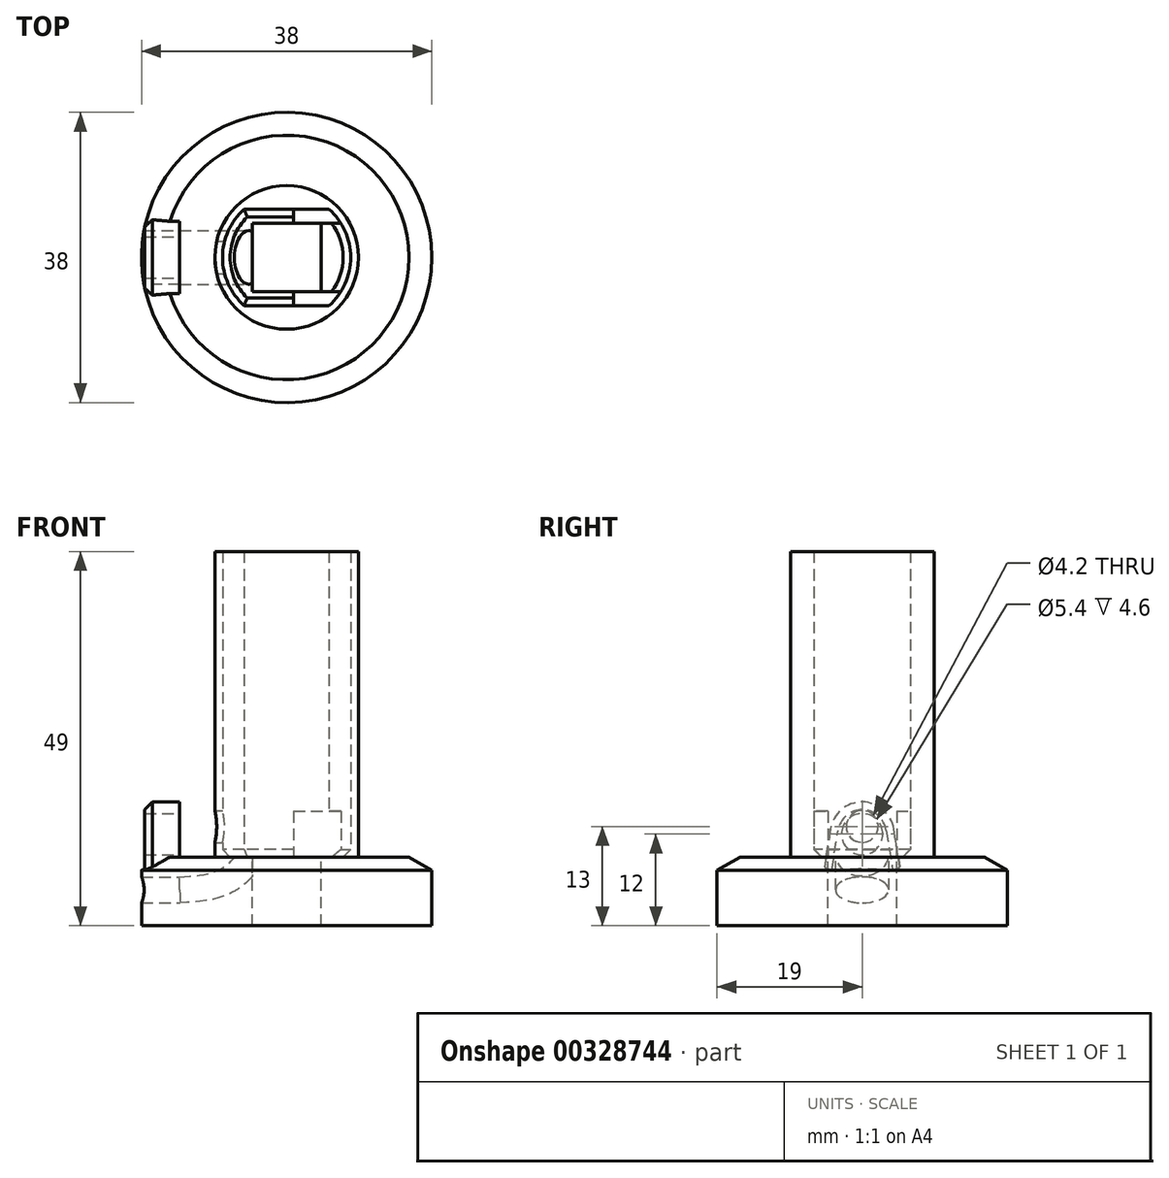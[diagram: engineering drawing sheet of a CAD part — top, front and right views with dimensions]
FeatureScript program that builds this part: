
annotation { "Feature Type Name" : "Feature", "Feature Type Description" : "" }
export const myFeature = defineFeature(function(context is Context, id is Id, definition is map)
    precondition{}
    {
        {
            var Q0;
            Q0=qCreatedBy(makeId("Top.planeOp"),FACE);
            var sketch = newSketch(context, id + "F0", { "sketchPlane" : qUnion([Q0])});
            skArc(sketch, "E0", {"start": v(-5.56, 6.3) * mm, "mid": v(-8.4, 0) * mm, "end": v(-5.56, -6.3) * mm});
            skLineSegment(sketch, "E1", {"start": v(-5.56, -6.3) * mm, "end": v(5.56, -6.3) * mm});
            skLineSegment(sketch, "E2", {"start": v(5.56, 6.3) * mm, "end": v(-5.56, 6.3) * mm});
            skArc(sketch, "E3.trimOffspring", {"start": v(5.56, -6.3) * mm, "mid": v(8.4, 0) * mm, "end": v(5.56, 6.3) * mm});
            skCircle(sketch, "E4", {"center": v(0, 0) * mm, "radius": 9.4 * mm});
            skSolve(sketch);
        }
        {
            var Q0;
            Q0 = qSketchRegion(id + "F0", true);
            extrude(context, id + "F1", {"entities" : qUnion([Q0]), "depth" : 40 * mm});
        }
        {
            var Q0;
            Q0=qCreatedBy(makeId("Top.planeOp"),FACE);
            var sketch = newSketch(context, id + "F2", { "sketchPlane" : qUnion([Q0])});
            skCircle(sketch, "E5", {"center": v(0, 0) * mm, "radius": 19 * mm});
            skLineSegment(sketch, "E6.bottom", {"start": v(-4.5, 4.5) * mm, "end": v(4.5, 4.5) * mm});
            skLineSegment(sketch, "E6.top", {"start": v(-4.5, -4.5) * mm, "end": v(4.5, -4.5) * mm});
            skLineSegment(sketch, "E6.left", {"start": v(-4.5, 4.5) * mm, "end": v(-4.5, -4.5) * mm});
            skLineSegment(sketch, "E6.right", {"start": v(4.5, 4.5) * mm, "end": v(4.5, -4.5) * mm});
            skLineSegment(sketch, "E7", {"start": v(-4.5, 4.5) * mm, "end": v(4.5, -4.5) * mm, "construction": true});
            skSolve(sketch);
        }
        {
            var Q0;
            Q0 = qSketchRegion(id + "F2", true);
            extrude(context, id + "F3", {"entities" : qUnion([Q0]), "operationType" : NewBodyOperationType.ADD, "oppositeDirection" : true, "depth" : 9 * mm});
        }
        {
            var Q0;
            Q0=makeQuery(id+"F1.opExtrude","CAP_EDGE",EDGE,{"disambiguationData":[OSD([sQuery(id+"F0.wireOp",EDGE,"E0")])],"isStart":true});
            var Q1;
            Q1=makeQuery(id+"F1.opExtrude","CAP_EDGE",EDGE,{"disambiguationData":[OSD([sQuery(id+"F0.wireOp",EDGE,"E2")])],"isStart":true});
            var Q2;
            Q2=makeQuery(id+"F1.opExtrude","CAP_EDGE",EDGE,{"disambiguationData":[OSD([sQuery(id+"F0.wireOp",EDGE,"E3.trimOffspring")])],"isStart":true});
            var Q3;
            Q3=makeQuery(id+"F1.opExtrude","CAP_EDGE",EDGE,{"disambiguationData":[OSD([sQuery(id+"F0.wireOp",EDGE,"E1")])],"isStart":true});
            chamfer(context, id + "F4", {"entities" : qUnion([Q0, Q1, Q2, Q3]), "width" : 1 * mm, "tangentPropagation" : true});
        }
        {
            var Q0;
            Q0=qCreatedBy(makeId("Right.planeOp"),FACE);
            var sketch = newSketch(context, id + "F5", { "sketchPlane" : qUnion([Q0])});
            skCircle(sketch, "E8.cCircle", {"center": v(0, 4) * mm, "radius": 2.1 * mm});
            skSolve(sketch);
        }
        {
            var Q0;
            Q0 = qSketchRegion(id + "F5", true);
            extrude(context, id + "F6", {"entities" : qUnion([Q0]), "operationType" : NewBodyOperationType.REMOVE, "oppositeDirection" : true, "depth" : 25 * mm});
        }
        {
            var Q0;
            Q0=makeQuery(id+"F3.opExtrude","CAP_EDGE",EDGE,{"disambiguationData":[OSD([sQuery(id+"F2.wireOp",EDGE,"E5")])],"isStart":true});
            chamfer(context, id + "F7", {"entities" : qUnion([Q0]), "chamferType" : ChamferType.OFFSET_ANGLE, "width" : 3 * mm, "oppositeDirection" : false, "angle" : 30 * degree, "tangentPropagation" : true});
        }
        {
            var Q0;
            Q0=qCreatedBy(makeId("Right.planeOp"),FACE);
            cPlane(context, id + "F8", {"entities" : qUnion([Q0]), "cplaneType" : CPlaneType.OFFSET, "offset" : 19 * mm, "oppositeDirection" : true, "width" : 150 * mm, "height" : 150 * mm});
        }
        {
            var Q0;
            Q0=qCreatedBy(id+"F8.planeOp",FACE);
            var sketch = newSketch(context, id + "F9", { "sketchPlane" : qUnion([Q0])});
            skLineSegment(sketch, "E9", {"start": v(0, 0) * mm, "end": v(0, -4.3) * mm, "construction": true});
            skEllipse(sketch, "E10", {"center": v(0, -4.3) * mm, "majorRadius": 3.5 * mm, "minorRadius": 1.7 * mm, "majorAxis": v(-1, 0)});
            skSolve(sketch);
        }
        {
            var Q0;
            Q0=qCreatedBy(makeId("Front.planeOp"),FACE);
            var sketch = newSketch(context, id + "F10", { "sketchPlane" : qUnion([Q0])});
            skLineSegment(sketch, "E11", {"start": v(-19, -4.3) * mm, "end": v(-14, -4.3) * mm});
            skFitSpline(sketch, "E12", {"points": [v(-14, -4.3) * mm, v(-7.22, -2.71) * mm, v(-4.5, 0.94) * mm], "startDerivative": vector(22.35, 1.09) * mm, "endDerivative": vector(5.98, 14.7) * mm});
            skSolve(sketch);
        }
        {
            var Q0;
            Q0=makeQuery(id+"F9.imprint","IMPRINT",FACE,{"disambiguationData":[TD([[makeQuery(id+"F9.imprint","IMPRINT",EDGE,{"derivedFrom":sQuery(id+"F9.wireOp",EDGE,"E10")}),1.0]])]});
            var Q1;
            Q1=sQuery(id+"F10.wireOp",EDGE,"E11");
            var Q2;
            Q2=sQuery(id+"F10.wireOp",EDGE,"E12");
            sweep(context, id + "F11", {"operationType" : NewBodyOperationType.REMOVE, "profiles" : qUnion([Q0]), "path" : qUnion([Q1, Q2])});
        }
        {
            var Q0;
            Q0=qCreatedBy(makeId("Right.planeOp"),FACE);
            cPlane(context, id + "F12", {"entities" : qUnion([Q0]), "cplaneType" : CPlaneType.OFFSET, "offset" : 14 * mm, "oppositeDirection" : true, "width" : 150 * mm, "height" : 150 * mm});
        }
        {
            var Q0;
            Q0=qCreatedBy(id+"F12.planeOp",FACE);
            var sketch = newSketch(context, id + "F13", { "sketchPlane" : qUnion([Q0])});
            skLineSegment(sketch, "E13", {"start": v(0, 0) * mm, "end": v(0, 3) * mm});
            skCircle(sketch, "E14", {"center": v(0, 3) * mm, "radius": 2.7 * mm});
            skArc(sketch, "E15", {"start": v(4.15, 3.66) * mm, "mid": v(0, 7.2) * mm, "end": v(-4.15, 3.66) * mm});
            skLineSegment(sketch, "E16", {"start": v(0, 0) * mm, "end": v(0, -1.73) * mm});
            skLineSegment(sketch, "E17", {"start": v(5, -1.73) * mm, "end": v(-5, -1.73) * mm});
            skLineSegment(sketch, "E18", {"start": v(5, -1.73) * mm, "end": v(4.15, 3.66) * mm});
            skLineSegment(sketch, "E19", {"start": v(-5, -1.73) * mm, "end": v(-4.15, 3.66) * mm});
            skPoint(sketch, "E20.orphan", {"position": v(-4.2, 3) * mm});
            skPoint(sketch, "E21.orphan", {"position": v(4.2, 3) * mm});
            skSolve(sketch);
        }
        {
            var Q0;
            Q0 = qSketchRegion(id + "F13", true);
            extrude(context, id + "F14", {"entities" : qUnion([Q0]), "operationType" : NewBodyOperationType.ADD, "oppositeDirection" : true, "depth" : 4.6 * mm});
        }
        {
            var Q0;
            Q0=makeQuery(id+"F14.opExtrude","CAP_EDGE",EDGE,{"disambiguationData":[OSD([sQuery(id+"F13.wireOp",EDGE,"E15")])],"isStart":false});
            var Q1;
            Q1=makeQuery(id+"F14.opExtrude","CAP_EDGE",EDGE,{"disambiguationData":[OSD([sQuery(id+"F13.wireOp",EDGE,"mBPwjUWr-pTdr-WgdO-0FXO-sCMZVrisKc0V.left")])],"isStart":false});
            var Q2;
            Q2=makeQuery(id+"F14.opExtrude","CAP_EDGE",EDGE,{"disambiguationData":[OSD([sQuery(id+"F13.wireOp",EDGE,"mBPwjUWr-pTdr-WgdO-0FXO-sCMZVrisKc0V.right")])],"isStart":false});
            chamfer(context, id + "F15", {"entities" : qUnion([Q0, Q1, Q2]), "width" : 1 * mm, "tangentPropagation" : true});
        }
        {
            var Q0;
            {var subQ0=sQuery(id+"F2.wireOp",EDGE,"E5");Q0=makeQuery(id+"F3.boolean.opBoolean","SPLIT",FACE,{"disambiguationData":[TD([makeQuery(id+"F1.opExtrude","SWEPT_FACE",FACE,{"disambiguationData":[OSD([sQuery(id+"F0.wireOp",EDGE,"E4")])]})])],"derivedFrom":makeQuery(id+"F3.opExtrude","CAP_FACE",FACE,{"disambiguationData":[OSD([subQ0,sQuery(id+"F2.wireOp",EDGE,"E6.bottom"),sQuery(id+"F2.wireOp",EDGE,"E6.top"),sQuery(id+"F2.wireOp",EDGE,"E6.left"),sQuery(id+"F2.wireOp",EDGE,"E6.right")])],"isStart":true})});}
            cPlane(context, id + "F16", {"entities" : qUnion([Q0]), "cplaneType" : CPlaneType.OFFSET, "offset" : 0 * mm, "width" : 150 * mm, "height" : 150 * mm});
        }
        {
            var Q0;
            Q0=qCreatedBy(id+"F16.planeOp",FACE);
            var sketch = newSketch(context, id + "F17", { "sketchPlane" : qUnion([Q0])});
            skLineSegment(sketch, "E22.bottom", {"start": v(0.9, 4.5) * mm, "end": v(7.1, 4.5) * mm});
            skLineSegment(sketch, "E22.top", {"start": v(0.9, 6.3) * mm, "end": v(5.56, 6.3) * mm});
            skLineSegment(sketch, "E22.left", {"start": v(0.9, 4.5) * mm, "end": v(0.9, 6.3) * mm});
            skLineSegment(sketch, "E23", {"start": v(-40, 0) * mm, "end": v(47.05, 0) * mm, "construction": true});
            skLineSegment(sketch, "E24.MirrorCS", {"start": v(0.9, -4.5) * mm, "end": v(7.1, -4.5) * mm});
            skLineSegment(sketch, "E25.MirrorCS", {"start": v(0.9, -4.5) * mm, "end": v(0.9, -6.3) * mm});
            skLineSegment(sketch, "E26.MirrorCS", {"start": v(0.9, -6.3) * mm, "end": v(5.56, -6.3) * mm});
            skArc(sketch, "E27", {"start": v(5.56, -6.3) * mm, "mid": v(6.39, -5.45) * mm, "end": v(7.1, -4.5) * mm});
            skArc(sketch, "E28.trimOffspring", {"start": v(7.1, 4.5) * mm, "mid": v(6.39, 5.45) * mm, "end": v(5.56, 6.3) * mm});
            skSolve(sketch);
        }
        {
            var Q0;
            Q0 = qSketchRegion(id + "F17", true);
            extrude(context, id + "F18", {"entities" : qUnion([Q0]), "operationType" : NewBodyOperationType.ADD, "depth" : 6 * mm});
        }
    });
